# Revit family: Kitchen_Taps-Mixers_hansgrohe_04827USA-Locarno-Single-lever-kitchen-mi_1
name_source: partatom
category: Plumbing Fixtures
revit_build: Autodesk Revit 2015 (Build: 20140903_1530(x64)
units: mm (PartAtom-declared; Revit-internal decimal feet)

## types (5) — shared parameters
Always visible = Yes
BIMobject category = Taps & Mixers
BIMobject category code = kitchen-taps
BIMobject main category = Kitchen
BIMobject main category code = kitchen
Brand url = http://www.hansgrohe-int.com
Design country = Germany
Edition number = 1
GTIN code = https://4059625310632
IFC Classification = Sanitary Terminal
Installation instructions = https://www.hansgrohe.com
Manufacturer country = Germany
Manufacturer name = hansgrohe
Material main = Chrome
Nominal height = 441.452 mm
Nominal width = 114.3 mm
Product Guid = efff0ea0-366c-4ec1-ba38-a9df7b0f2929
Product SKU = 04827USA
Product data url = https://bimobject.com
Product family = Locarno
Product group = Kitchen mixers
Product url = https://www.hansgrohe.com
QR code = http://bimobject.com
Technical description = https://www.hansgrohe.com
Weight Net (Kg) = 0

## per-type parameters (varying)
| type | Material 1 |
| 000 Chrome | Hansgrohe - Locarno - 000 Chrome |
| 250 Brushed Gold Optic | Hansgrohe - Locarno - 250 Brushed Gold Optic |
| 670 Matte Black | Hansgrohe - Locarno - 670 Matte Black |
| 800 Stainless Steel Optic | Hansgrohe - Locarno - 800 Stainless Steel Optic |
| 830 Polished Nickel | Hansgrohe - Locarno - 830 Polished Nickel |

## geometry (parser evidence)
native form markers: Sweep x2
no freeform markers — native parametric forms only
